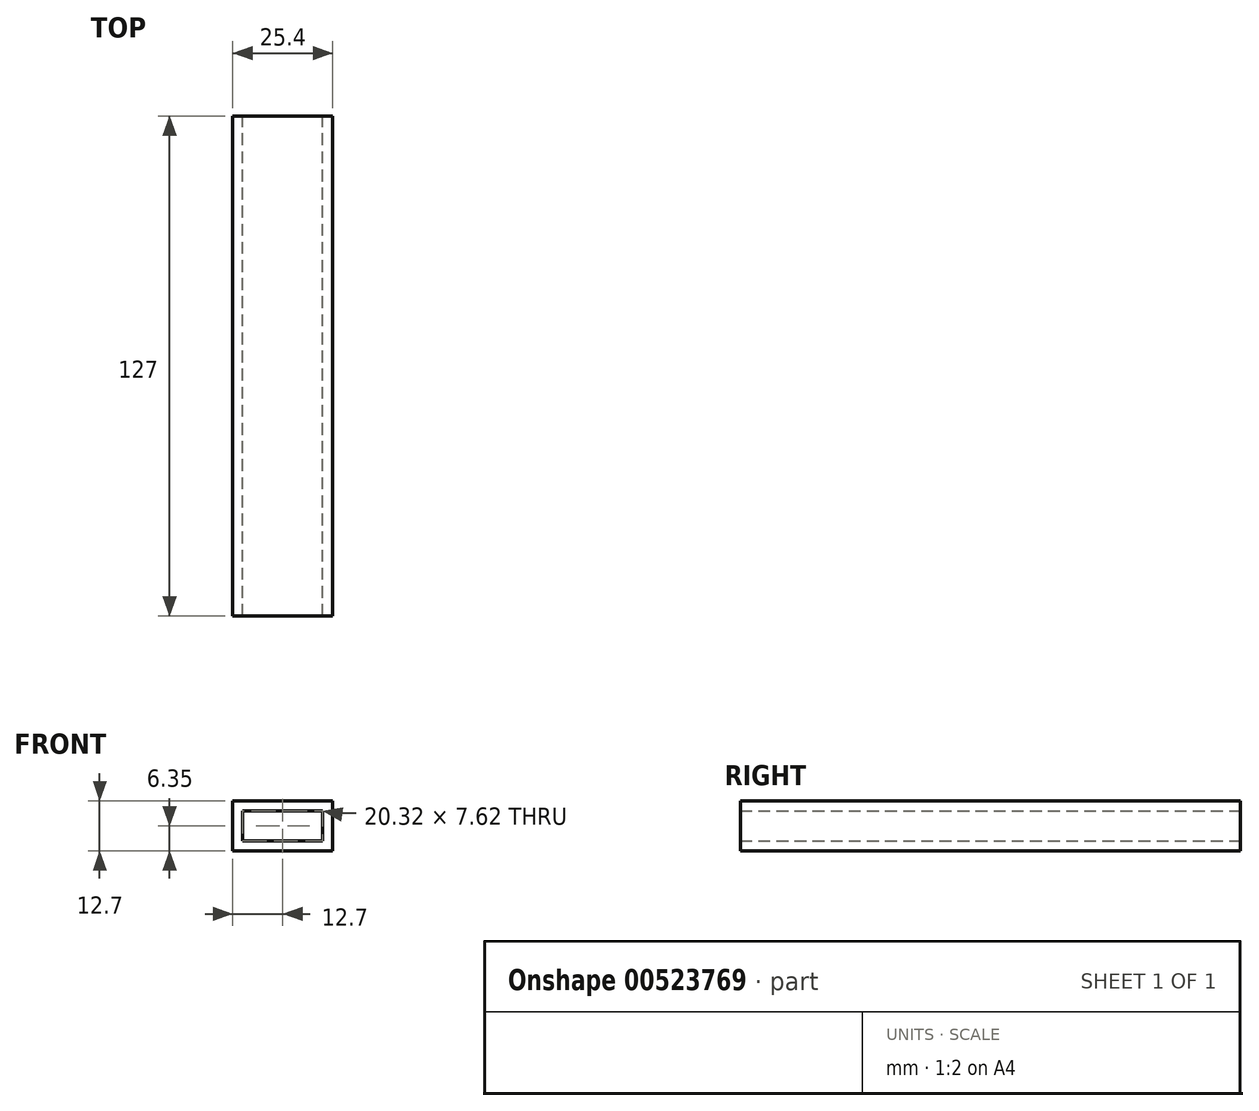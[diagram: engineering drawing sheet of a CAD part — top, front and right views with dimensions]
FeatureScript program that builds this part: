
annotation { "Feature Type Name" : "Feature", "Feature Type Description" : "" }
export const myFeature = defineFeature(function(context is Context, id is Id, definition is map)
    precondition{}
    {
        {
            var Q0;
            Q0=qCreatedBy(makeId("Front.planeOp"),FACE);
            var sketch = newSketch(context, id + "F0", { "sketchPlane" : qUnion([Q0])});
            skLineSegment(sketch, "E0", {"start": v(0, 0) * mm, "end": v(-25.4, 0) * mm});
            skLineSegment(sketch, "E1", {"start": v(-25.4, 0) * mm, "end": v(-25.4, 12.7) * mm});
            skLineSegment(sketch, "E2", {"start": v(-25.4, 12.7) * mm, "end": v(0, 12.7) * mm});
            skLineSegment(sketch, "E3", {"start": v(0, 12.7) * mm, "end": v(0, 0) * mm});
            skLineSegment(sketch, "E4", {"start": v(-25.4, 12.7) * mm, "end": v(-22.86, 12.7) * mm});
            skLineSegment(sketch, "E5", {"start": v(-22.86, 12.7) * mm, "end": v(-22.86, 10.16) * mm});
            skLineSegment(sketch, "E6.bottom", {"start": v(-22.86, 10.16) * mm, "end": v(-2.54, 10.16) * mm});
            skLineSegment(sketch, "E6.top", {"start": v(-22.86, 2.54) * mm, "end": v(-2.54, 2.54) * mm});
            skLineSegment(sketch, "E6.left", {"start": v(-22.86, 10.16) * mm, "end": v(-22.86, 2.54) * mm});
            skLineSegment(sketch, "E6.right", {"start": v(-2.54, 10.16) * mm, "end": v(-2.54, 2.54) * mm});
            skSolve(sketch);
        }
        {
            var Q0;
            Q0=makeQuery(id+"F0.imprint","IMPRINT",FACE,{"disambiguationData":[TD([[makeQuery(id+"F0.imprint","IMPRINT",EDGE,{"derivedFrom":sQuery(id+"F0.wireOp",EDGE,"E0")}),-1.0]])]});
            extrude(context, id + "F1", {"entities" : qUnion([Q0]), "depth" : 127 * mm, "offsetDistance" : 25.4 * mm});
        }
    });
